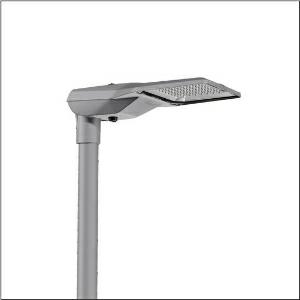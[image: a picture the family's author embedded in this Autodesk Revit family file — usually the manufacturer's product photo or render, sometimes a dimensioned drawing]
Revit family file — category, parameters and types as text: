
# Revit family: streetlight_sl_21_iq_midi___st1_0ab_5xe3m31y08mb_ceed
name_source: partatom
category: Lighting Fixtures
units: mm (PartAtom-declared; Revit-internal decimal feet)

## family parameters
Cut with Voids When Loaded = No
Host = Face
Light Source = No
Part Type = Normal
Room Calculation Point = No
Round Connector Dimension = Use Diameter
Shared = No

## types (1)
- --- (1 x LED, 16140 lm, 129.3 W, 3000K)
    Apparent Load = 129 VA
    CIE Flux Codes = 38 73 97 100 100
    Color Rendering = 70
    Color Temperature = 3000K
    Default Elevation = 1800 mm
    Description = Streetlight SL 21 iQ midi, mast luminaire, primary light control with lens, of PMMA, primary optical cover: cover, of toughened safety glass, transparent, light distribution: ST1.0aB, light emission: direct distribution, primary light characteristic: asymmetric, installation type: post-top, side-entry, LED, High Power LED, rated luminous flux: 16.140lm, luminous efficacy: 125lm/W, light colour: 730, colour temperature: 3000K, control gear: iQ-Street Remote, D4i with power reduction, control: pre-setting: logarithmic dimming characteristic, Street-Remote, Auto-Match, Temp-Guard, Lumen-Switch, Night-Set, Smart-Wire, Light-Fading, Desk-Remote (wireless, voltage-free reading and setting of iQ features in the workshop via application-optimized NFC function/RFID function), optimised constant luminous flux control (CLO 2.0), mains connection: 230..240V, AC, 50/60Hz, start of lifetime: 129W, end of service life: 142W, reduction: 56W, luminaire housing, of diecast aluminium, powder-coated, Siteco® metallic grey (DB 702S), corrosivity category C5 mid according to DIN EN ISO 12944, please order mast flange separately, inclination adjustable: 0°, 5°, 10°, 15°, sealing non-destructively replaceable, multi-level sealing system, length: 644mm, width: 335mm, height: 110mm, mast flange for spigot size: 42mm (side-entry): 5XC10008XM4, 60/48mm (side-entry/post-top): 5XC10108XM2, 76/60mm (side-entry/post-top): 5XC10108XM1, mounting height: 4..8m, Smart Interface below and above, protection rating (complete): IP66, insulation class (complete): insulation class II (safety insulation), certification: CE, ENEC, ENEC+, VDE, impact resistance: IK10, permissible operating ambient temperature for outdoor applications: -40..+50°C, standard-compliant lighting for roads and squares, packaging unit: 1 piece

Light Distribution: ST1.0aB
    Height = 111 mm
    Lamp = 1 x LED
    Lamp Light Flux = 16140 lm
    Lamp Power = 129.3 W
    Lamp count = 1
    Length = 644 mm
    Luminous efficacy = 125 lm/W
    Manufacturer = Siteco
    ModVariant = No
    Model = 5XE3M31Y08MB
    Number of Poles = 1
    OnlyDefault = Yes
    Power Factor = 1
    Product Name = Streetlight SL 21 iQ midi | ST1.0aB
    Product group = mast luminaire | pylon top
    ProductGroupID = 6100
    Protection Class = Protection class II
    Protection Degree = IP 66
    RLX_Detail_Level = 1
    RLX_Emergency_Light_Flux = 0 lm
    RLX_Emergency_Type = 0
    RLX_Emergency_Type_DB = No
    RlxData = <blob elided: 91173 chars, md5=a64bac17>
    Socket = socket
    Standby Power = 0 W
    System Light Flux = 16141 lm
    System Power = 129 W
    Type Comments = factory setting: luminous flux: 100 % | dim-lin: 254 | 672 mA
    Type Image = l_1004304.jpg
    URL = http://relux.com
    VarID = @adj_133763
    Voltage = 0 V
    Weight = 0.00 kg
    Width = 336 mm

## geometry (parser evidence)
native form markers: Blend x4, Sweep x11
no freeform markers — native parametric forms only
